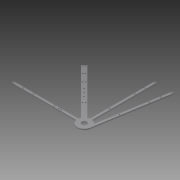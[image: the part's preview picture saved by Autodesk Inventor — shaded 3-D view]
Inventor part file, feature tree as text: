
AUTODESK INVENTOR PART (.ipt)
format: ipt  version: 2013 (Build 170138000, 138)  size: 218,112 bytes
history: native  units: in
note: dims shown in document units (in); Inventor stores cm internally (conversion verified against a paired STEP export)
features: extrude x2, sketch x2
ambient origin geometry x8: Origin, YZ Plane, XZ Plane, XY Plane, X Axis, Y Axis, Z Axis, Center Point
feature tree (4):
  extrude  "Extrusion2"  Depth=1.5in
  extrude  "Extrusion8"  Depth=0.25in
  sketch  "Sketch1"  dims[d0=0.5in d1=4.0in d2=0.5in d3=0.5in d4=1.5in d5=1.5in d6=1.5in d7=0.25in d8=0.25in d9=0.25in d10=0.5in d11=0.5in d12=3.75in d14=0.266in d15=0.266in d16=0.266in d17=0.25in d18=0.266in d19=0.25in d20=0.25in d21=0.266in d22=0.266in d23=0.266in d24=0.25in d25=0.25in d26=0.266in d28=1.125in d30=0.266in d32=0.266in d33=0.25in d36=1.5in]
  sketch  "Sketch6"  dims[d37=1.0in d38=0.25in d39=5.5in d40=2.1762in d41=5.5in d42=0.25in d43=0.25in d44=0.2874in d45=10.926in d46=10.6389in d47=0.2871in d48=0.2871in d49=15.5in d50=15.5in d51=0.25in d52=0.5in d53=0.266in d54=0.25in d55=0.266in d56=0.266in d57=15.5in d58=0.25in d60=0.266in d61=0.25in d62=0.266in d63=0.266in d64=0.266in d65=0.266in d66=2.0in d67=2.0in d68=2.0in d71=0.297in d72=0.297in d73=0.297in d74=0.297in d75=2.0in d77=0.0in d78=0.25in d79=0.25in d80=0.0in d115=0.266in d117=0.266in d118=9.75in d122=6.0in d123=8.0in d124=0.266in d126=6.0in d127=8.0in d129=0.25in d130=0.25in d131=0.25in d132=0.25in d133=1.0in d134=0.0in]
